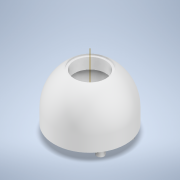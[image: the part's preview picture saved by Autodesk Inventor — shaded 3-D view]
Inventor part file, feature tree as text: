
AUTODESK INVENTOR PART (.ipt)
format: ipt  version: 2021 (Build 250183000, 183)  size: 420,864 bytes
history: native  units: in
note: dims shown in document units (in); Inventor stores cm internally (conversion verified against a paired STEP export)
features: sketch x6, extrude x5, other x1, revolve x1, pattern_circular x1, mirror x1, fillet x1
ambient origin geometry x8: Origin, YZ Plane, XZ Plane, XY Plane, X Axis, Y Axis, Z Axis, Center Point
bodies: Solid1 (feature_tree)
feature tree (16):
  extrude  "Extrusion1"  Depth=1.0236in
  other  "Work Axis1"
  revolve  "Revolution1"  [1 undecoded]
  extrude  "Extrusion2"  Depth=1.0079in
  extrude  "Extrusion3"  TaperAngle=90.0deg  [1 undecoded]
  extrude  "Extrusion4"  Depth=0.8976in
  extrude  "Extrusion5"  Depth=1.0236in TaperAngle=0.0deg
  pattern_circular  "Circular Pattern1"  [2 undecoded]
  mirror  "Mirror1"
  fillet  "Fillet2"  Radius=0.2126in
  sketch  "Sketch1"  dims[d0=2.0472in d1=1.0236in]
  sketch  "Sketch2"  dims[d2=1.0236in d3=1.0236in]
  sketch  "Sketch3"  dims[d4=1.378in d5=0.0in d6=1.0079in]
  sketch  "Sketch4"  dims[d7=90.0deg d8=90.0deg]
  sketch  "Sketch5"  dims[d9=0.0394in d10=0.0in d11=0.8976in]
  sketch  "Sketch8"  dims[d12=0.0in d13=0.0in d14=1.0236in d15=0.0in d16=1.2913in d21=0.2126in d22=0.8268in d23=0.1969in d24=0.0in d25=1.9685in d26=240.0deg d33=0.5039in d34=0.0394in]
note: 4 required parameter values undecoded (feature->parameter linkage not recoverable at this tier; creation-order binding heuristic only, values carry confidence <= 0.55)